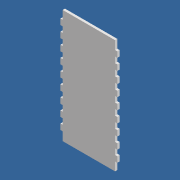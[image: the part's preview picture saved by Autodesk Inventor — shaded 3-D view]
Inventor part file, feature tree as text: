
AUTODESK INVENTOR PART (.ipt)
format: ipt  version: 2021 (Build 250183000, 183)  size: 230,912 bytes
history: native  units: mm
features: extrude x3, sketch x3, other x1
ambient origin geometry x8: Origin, YZ Plane, XZ Plane, XY Plane, X Axis, Y Axis, Z Axis, Center Point
bodies: Solid1 (feature_tree)
feature tree (7):
  other  "<userpath>\OneDrive\Objet3D\Clawd3\parameters.xlsx"
  extrude  "Extrusion1"  Depth=300.0mm
  extrude  "Extrusion2"  TaperAngle=0.0deg  [1 undecoded]
  extrude  "Extrusion3"  Depth=5.9mm
  sketch  "Sketch1"  dims[d0=162.0mm d1=300.0mm]
  sketch  "Sketch2"  dims[d2=6.0mm d3=0.0mm]
  sketch  "Sketch3"  dims[d4=0.0mm d5=5.9mm d6=0.0mm d7=22.5mm d8=5.9mm d9=15.0mm d10=15.0mm d11=80.0mm d13=30.0mm d14=10.0mm d16=10.0mm d18=22.5mm d19=5.9mm d20=24.0mm d21=0.0mm d22=5.0mm d23=5.0mm d24=5.0mm d25=5.0mm d26=5.0mm d27=5.0mm d28=5.0mm d29=5.0mm d30=105.0mm d31=105.0mm d32=105.0mm d33=22.5mm d34=150.2mm d35=105.0mm d36=105.0mm d37=105.0mm d38=30.0mm d39=22.5mm d40=30.0mm d41=105.0mm d42=24.0mm d43=0.0mm d44=135.0mm d45=30.0mm d46=82.5mm d47=75.1mm d48=75.1mm]
note: 1 required parameter value undecoded (feature->parameter linkage not recoverable at this tier; creation-order binding heuristic only, values carry confidence <= 0.55)
